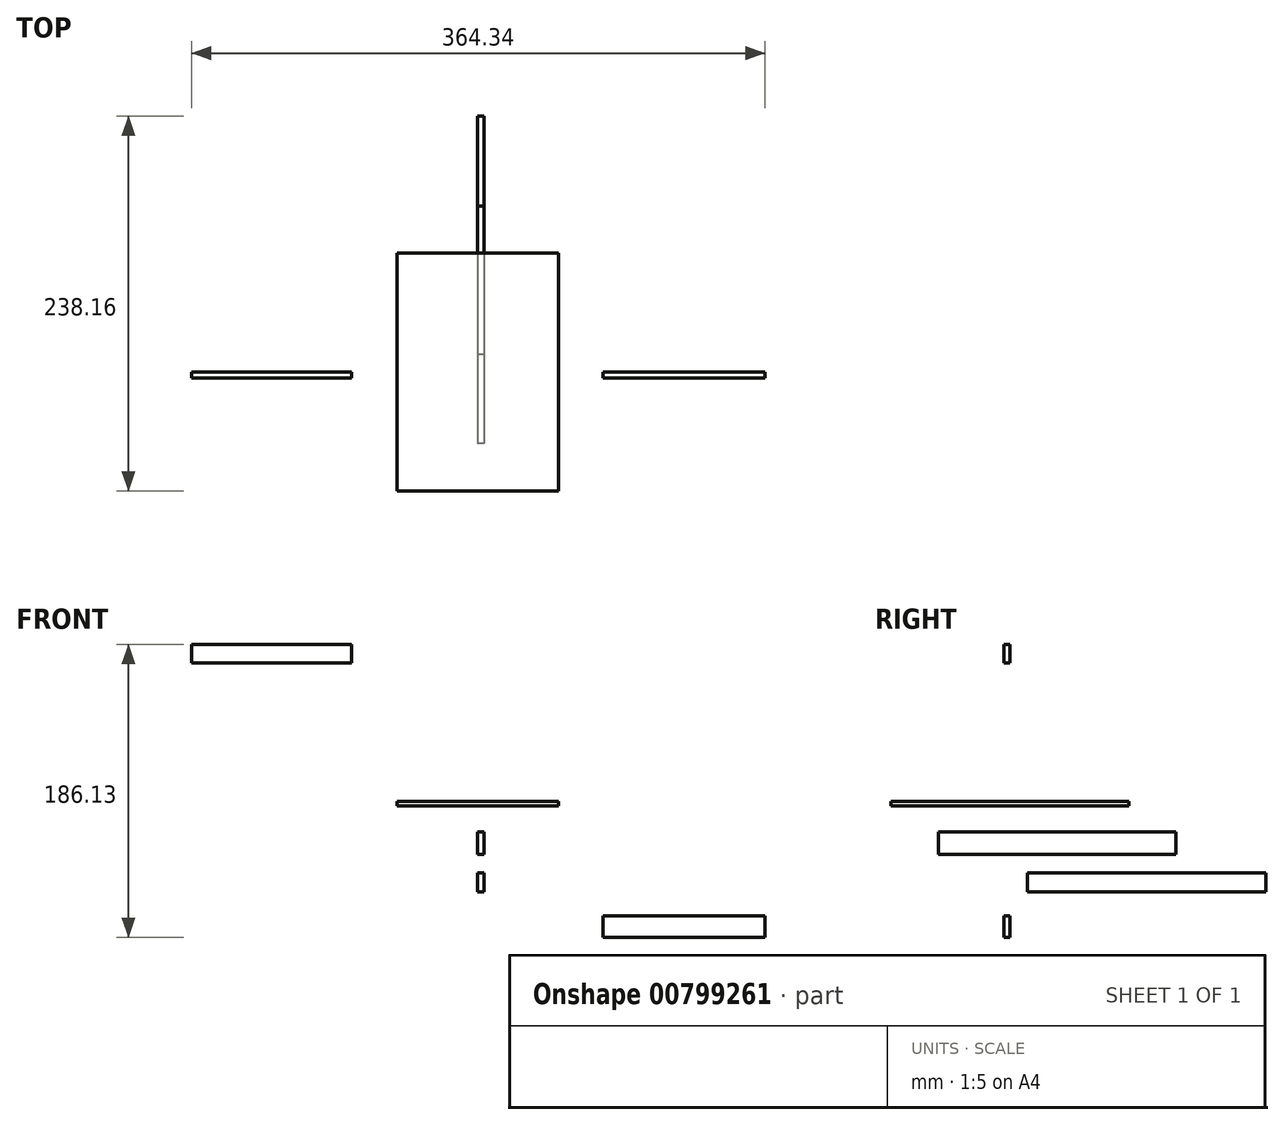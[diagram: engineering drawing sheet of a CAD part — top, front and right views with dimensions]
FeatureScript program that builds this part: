
annotation { "Feature Type Name" : "Feature", "Feature Type Description" : "" }
export const myFeature = defineFeature(function(context is Context, id is Id, definition is map)
    precondition{}
    {
        {
            var Q0;
            Q0=qCreatedBy(makeId("Top.planeOp"),FACE);
            var sketch = newSketch(context, id + "F0", { "sketchPlane" : qUnion([Q0])});
            skLineSegment(sketch, "E0.bottom", {"start": v(-51.37, -75.59) * mm, "end": v(51.37, -75.59) * mm});
            skLineSegment(sketch, "E0.top", {"start": v(-51.37, 75.59) * mm, "end": v(51.37, 75.59) * mm});
            skLineSegment(sketch, "E0.left", {"start": v(-51.37, -75.59) * mm, "end": v(-51.37, 75.59) * mm});
            skLineSegment(sketch, "E0.right", {"start": v(51.37, -75.59) * mm, "end": v(51.37, 75.59) * mm});
            skPoint(sketch, "E0.middle", {"position": v(0, 0) * mm});
            skSolve(sketch);
        }
        {
            var Q0;
            Q0 = qSketchRegion(id + "F0", true);
            extrude(context, id + "F1", {"entities" : qUnion([Q0]), "depth" : 2.8 * mm, "offsetDistance" : 25 * mm});
        }
        {
            var Q0;
            Q0=qCreatedBy(makeId("Right.planeOp"),FACE);
            var sketch = newSketch(context, id + "F2", { "sketchPlane" : qUnion([Q0])});
            skLineSegment(sketch, "E1.bottom", {"start": v(105.4, -30.94) * mm, "end": v(-45.6, -30.94) * mm});
            skLineSegment(sketch, "E1.top", {"start": v(105.4, -16.74) * mm, "end": v(-45.6, -16.74) * mm});
            skLineSegment(sketch, "E1.left", {"start": v(105.4, -30.94) * mm, "end": v(105.4, -16.74) * mm});
            skLineSegment(sketch, "E1.right", {"start": v(-45.6, -30.94) * mm, "end": v(-45.6, -16.74) * mm});
            skSolve(sketch);
        }
        {
            var Q0;
            Q0 = qSketchRegion(id + "F2", true);
            extrude(context, id + "F3", {"entities" : qUnion([Q0]), "depth" : 4 * mm, "offsetDistance" : 25 * mm});
        }
        {
            var Q0;
            Q0=qCreatedBy(makeId("Right.planeOp"),FACE);
            var sketch = newSketch(context, id + "F4", { "sketchPlane" : qUnion([Q0])});
            skLineSegment(sketch, "E2.bottom", {"start": v(162.57, -54.86) * mm, "end": v(11.04, -54.86) * mm});
            skLineSegment(sketch, "E2.top", {"start": v(162.57, -42.6) * mm, "end": v(11.04, -42.6) * mm});
            skLineSegment(sketch, "E2.left", {"start": v(162.57, -54.86) * mm, "end": v(162.57, -42.6) * mm});
            skLineSegment(sketch, "E2.right", {"start": v(11.04, -54.86) * mm, "end": v(11.04, -42.6) * mm});
            skSolve(sketch);
        }
        {
            var Q0;
            Q0 = qSketchRegion(id + "F4", true);
            extrude(context, id + "F5", {"entities" : qUnion([Q0]), "depth" : 4 * mm, "offsetDistance" : 25 * mm});
        }
        {
            var Q0;
            Q0=qCreatedBy(makeId("Front.planeOp"),FACE);
            var sketch = newSketch(context, id + "F6", { "sketchPlane" : qUnion([Q0])});
            skLineSegment(sketch, "E3.bottom", {"start": v(79.66, -83.7) * mm, "end": v(182.5, -83.7) * mm});
            skLineSegment(sketch, "E3.top", {"start": v(79.66, -70.09) * mm, "end": v(182.5, -70.09) * mm});
            skLineSegment(sketch, "E3.left", {"start": v(79.66, -83.7) * mm, "end": v(79.66, -70.09) * mm});
            skLineSegment(sketch, "E3.right", {"start": v(182.5, -83.7) * mm, "end": v(182.5, -70.09) * mm});
            skSolve(sketch);
        }
        {
            var Q0;
            Q0=makeQuery(id+"F6.imprint","IMPRINT",FACE,{"disambiguationData":[TD([[makeQuery(id+"F6.imprint","IMPRINT",EDGE,{"derivedFrom":sQuery(id+"F6.wireOp",EDGE,"E3.bottom")}),1.0]])]});
            extrude(context, id + "F7", {"entities" : qUnion([Q0]), "depth" : 4 * mm, "offsetDistance" : 25 * mm});
        }
        {
            var Q0;
            Q0=qCreatedBy(makeId("Front.planeOp"),FACE);
            var sketch = newSketch(context, id + "F8", { "sketchPlane" : qUnion([Q0])});
            skLineSegment(sketch, "E4.bottom", {"start": v(-181.84, 90.6) * mm, "end": v(-79.98, 90.6) * mm});
            skLineSegment(sketch, "E4.top", {"start": v(-181.84, 102.43) * mm, "end": v(-79.98, 102.43) * mm});
            skLineSegment(sketch, "E4.left", {"start": v(-181.84, 90.6) * mm, "end": v(-181.84, 102.43) * mm});
            skLineSegment(sketch, "E4.right", {"start": v(-79.98, 90.6) * mm, "end": v(-79.98, 102.43) * mm});
            skSolve(sketch);
        }
        {
            var Q0;
            Q0 = qSketchRegion(id + "F8", true);
            extrude(context, id + "F9", {"entities" : qUnion([Q0]), "depth" : 4 * mm, "offsetDistance" : 25 * mm});
        }
    });
